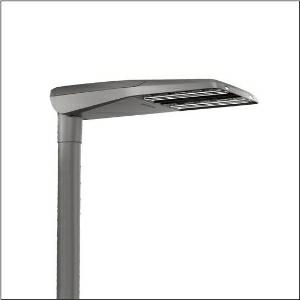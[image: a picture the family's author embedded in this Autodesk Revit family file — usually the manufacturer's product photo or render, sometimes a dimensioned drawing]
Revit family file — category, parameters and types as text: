
# Revit family: streetlight_sl_11_iq_midi___pc-r_5xc3f51e08me_15a1
name_source: partatom
category: Lighting Fixtures
units: mm (PartAtom-declared; Revit-internal decimal feet)

## family parameters
Cut with Voids When Loaded = No
Host = Face
Light Source = No
Part Type = Normal
Room Calculation Point = No
Round Connector Dimension = Use Diameter
Shared = No

## types (1)
- --- (1 x LED, 15540 lm, 124.7 W, 3000K)
    Apparent Load = 125 VA
    CIE Flux Codes = 37 73 96 100 100
    Color Rendering = 70
    Color Temperature = 3000K
    Default Elevation = 1800 mm
    Description = Streetlight SL 11 iQ midi, mast luminaire, primary light control with 3 zone facetted reflector, of plastic, silver coated, highly specular, primary optical cover: cover, of PMMA, transparent, light distribution: PC-R, light emission: direct distribution, primary light characteristic: asymmetric, installation type: post-top, side-entry, LED, High Power LED, rated luminous flux: 15.540lm, luminous efficacy: 125lm/W, light colour: 730, colour temperature: 3000K, control: optimised constant luminous flux control (CLO 2.0), Desk-Remote (wireless, voltage-free reading and setting of iQ features in the workshop via application-optimized NFC function/RFID function), Light-Fading, Smart-Wire, Night-Set, Lumen-Switch, Temp-Guard, Auto-Match, with cable H07RN-F 5x 1.5mm², mains connection: 220..240V, AC, 50/60Hz, connection cable pre-assembled, cable length: 12,5m, start of lifetime: 125W, end of lifetime: 132W, reduction: 61W, luminaire housing, of diecast aluminium, powder-coated, Siteco® metallic grey (DB 702S), length: 780mm, width: 376mm, height: 118mm, spigot size: 60/76mm (post-top) and 42/60/76mm (side-entry), mast flange for spigot size: 42mm: 5XC10008XM4, 60mm: 5XC10008XM2, 76/60mm: 5XC10108XM1, equipment: Power, protection rating (complete): IP66, insulation class (complete): insulation class II (safety insulation), certification: CE, ENEC, VDE, impact resistance: IK09, permissible operating ambient temperature for outdoor applications: -25..+50°C, standard-compliant lighting for roads and squares, packaging unit: 1 piece

Light Distribution: PC-R
    Height = 118 mm
    Lamp = 1 x LED
    Lamp Light Flux = 15540 lm
    Lamp Power = 124.7 W
    Lamp count = 1
    Length = 780 mm
    Luminous efficacy = 125 lm/W
    Manufacturer = Siteco
    ModVariant = No
    Model = 5XC3F51E08ME
    Number of Poles = 1
    OnlyDefault = Yes
    Power Factor = 1
    Product Name = Streetlight SL 11 iQ midi | PC-R
    Product group = mast luminaire | pylon top
    ProductGroupID = 6100
    Protection Class = Protection class II
    Protection Degree = IP 66
    RLX_Detail_Level = 1
    RlxData = <blob elided: 74101 chars, md5=44e17bf6>
    Socket = socket
    Standby Power = 0 W
    System Light Flux = 15540 lm
    System Power = 125 W
    Type Comments = factory setting: luminous flux: 100 % | dim-lin: 254 | 557 mA
    Type Image = l_1005960.jpg
    URL = http://relux.com
    VarID = @adj_117665
    Voltage = 0 V
    Weight = 0.00 kg
    Width = 376 mm

## geometry (parser evidence)
native form markers: Blend x4, Sweep x10
no freeform markers — native parametric forms only
